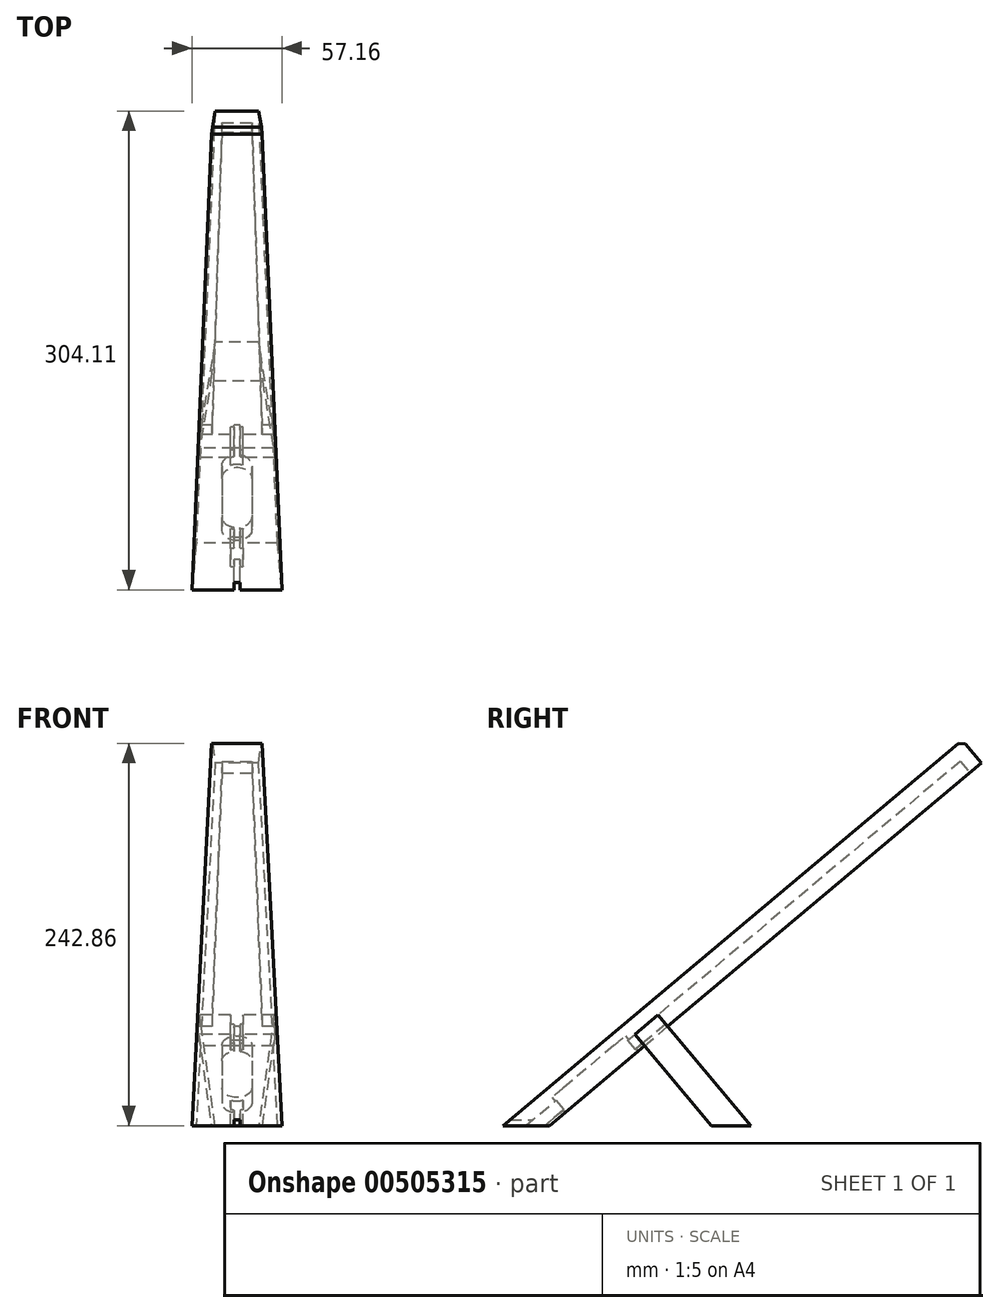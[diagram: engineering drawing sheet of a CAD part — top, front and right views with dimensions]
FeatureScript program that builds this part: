
annotation { "Feature Type Name" : "Feature", "Feature Type Description" : "" }
export const myFeature = defineFeature(function(context is Context, id is Id, definition is map)
    precondition{}
    {
        {
            var Q0;
            Q0=qCreatedBy(makeId("Right.planeOp"),FACE);
            var sketch = newSketch(context, id + "F0", { "sketchPlane" : qUnion([Q0])});
            skLineSegment(sketch, "E0", {"start": v(-81.13, 0) * mm, "end": v(210.73, 244.9) * mm});
            skLineSegment(sketch, "E1", {"start": v(210.73, 244.9) * mm, "end": v(222.98, 230.3) * mm});
            skLineSegment(sketch, "E2", {"start": v(222.98, 230.3) * mm, "end": v(23.54, 62.96) * mm});
            skLineSegment(sketch, "E3", {"start": v(-51.5, 0) * mm, "end": v(-81.13, 0) * mm});
            skLineSegment(sketch, "E4", {"start": v(8.94, 50.71) * mm, "end": v(51.5, 0) * mm});
            skLineSegment(sketch, "E5", {"start": v(51.5, 0) * mm, "end": v(76.36, 0) * mm});
            skLineSegment(sketch, "E6", {"start": v(76.36, 0) * mm, "end": v(23.54, 62.96) * mm});
            skLineSegment(sketch, "E7.trimOffspring", {"start": v(8.94, 50.71) * mm, "end": v(-51.5, 0) * mm});
            skLineSegment(sketch, "E8", {"start": v(-28.8, 19.05) * mm, "end": v(35.51, 19.05) * mm});
            skLineSegment(sketch, "E9", {"start": v(-51.5, 0) * mm, "end": v(51.5, 0) * mm});
            skLineSegment(sketch, "E10", {"start": v(35.51, 19.05) * mm, "end": v(60.38, 19.05) * mm});
            skLineSegment(sketch, "E11", {"start": v(-28.8, 19.05) * mm, "end": v(-58.43, 19.05) * mm});
            skLineSegment(sketch, "E12", {"start": v(23.54, 62.96) * mm, "end": v(17.41, 70.26) * mm});
            skLineSegment(sketch, "E13", {"start": v(17.41, 70.26) * mm, "end": v(2.82, 58.01) * mm});
            skLineSegment(sketch, "E14", {"start": v(8.94, 50.71) * mm, "end": v(2.82, 58.01) * mm});
            skSolve(sketch);
        }
        {
            var Q0;
            Q0=makeQuery(id+"F0.imprint","IMPRINT",FACE,{"disambiguationData":[TD([[makeQuery(id+"F0.imprint","IMPRINT",EDGE,{"derivedFrom":sQuery(id+"F0.wireOp",EDGE,"E0")}),-1.0]])]});
            var Q1;
            {var subQ0=sQuery(id+"F0.wireOp",EDGE,"E1");Q1=makeQuery(id+"F0.imprint","IMPRINT",FACE,{"disambiguationData":[TD([[makeQuery(id+"F0.imprint","IMPRINT",EDGE,{"derivedFrom":subQ0}),-1.0]])]});}
            extrude(context, id + "F1", {"entities" : qUnion([Q0, Q1]), "depth" : 57.15 * mm, "symmetric" : true});
        }
        {
            var Q0;
            Q0=makeQuery(id+"F0.imprint","IMPRINT",FACE,{"disambiguationData":[TD([[makeQuery(id+"F0.imprint","IMPRINT",EDGE,{"derivedFrom":sQuery(id+"F0.wireOp",EDGE,"E4")}),1.0]])]});
            var Q1;
            {var subQ1=sQuery(id+"F0.wireOp",EDGE,"EqHhwjUs-oOLM-PdHP-ePqw-IKI6tSrCbLh4");Q1=makeQuery(id+"F0.imprint","IMPRINT",FACE,{"disambiguationData":[TD([[makeQuery(id+"F0.imprint","IMPRINT",EDGE,{"derivedFrom":subQ1}),1.0]])]});}
            var Q2;
            {var subQ3=sQuery(id+"F0.wireOp",EDGE,"E10");Q2=makeQuery(id+"F0.imprint","IMPRINT",FACE,{"disambiguationData":[TD([[makeQuery(id+"F0.imprint","IMPRINT",EDGE,{"derivedFrom":subQ3}),1.0]])]});}
            extrude(context, id + "F2", {"entities" : qUnion([Q0, Q1, Q2]), "depth" : 57.15 * mm, "symmetric" : true});
        }
        {
            var Q0;
            Q0=makeQuery(id+"F1.opExtrude","SWEPT_FACE",FACE,{"disambiguationData":[OSD([sQuery(id+"F0.wireOp",EDGE,"E0")])]});
            var sketch = newSketch(context, id + "F3", { "sketchPlane" : qUnion([Q0])});
            skLineSegment(sketch, "E15", {"start": v(-15.87, 318.85) * mm, "end": v(-28.58, -62.15) * mm});
            skLineSegment(sketch, "E16", {"start": v(-28.58, -62.15) * mm, "end": v(-28.58, 318.85) * mm});
            skLineSegment(sketch, "E17", {"start": v(-28.58, 318.85) * mm, "end": v(-15.87, 318.85) * mm});
            skLineSegment(sketch, "E18.MirrorCS", {"start": v(15.87, 318.85) * mm, "end": v(28.58, -62.15) * mm});
            skLineSegment(sketch, "E19.MirrorCS", {"start": v(28.58, 318.85) * mm, "end": v(15.87, 318.85) * mm});
            skLineSegment(sketch, "E20.MirrorCS", {"start": v(28.58, -62.15) * mm, "end": v(28.58, 318.85) * mm});
            skSolve(sketch);
        }
        {
            var Q0;
            Q0=makeQuery(id+"F1.opExtrude","SWEPT_FACE",FACE,{"disambiguationData":[OSD([sQuery(id+"F0.wireOp",EDGE,"E2")])]});
            var sketch = newSketch(context, id + "F4", { "sketchPlane" : qUnion([Q0])});
            skLineSegment(sketch, "E21", {"start": v(15.87, -58.5) * mm, "end": v(-15.87, -58.5) * mm});
            skLineSegment(sketch, "E22", {"start": v(-9.52, -309.32) * mm, "end": v(9.52, -309.32) * mm});
            skLineSegment(sketch, "E23", {"start": v(0, -318.85) * mm, "end": v(0, -309.32) * mm, "construction": true});
            skLineSegment(sketch, "E24", {"start": v(0, -309.32) * mm, "end": v(0, -318.85) * mm, "construction": true});
            skArc(sketch, "E25", {"start": v(-9.53, -24.69) * mm, "mid": v(0, -34.21) * mm, "end": v(9.53, -24.69) * mm});
            skArc(sketch, "E26", {"start": v(9.53, 17.22) * mm, "mid": v(0, 26.75) * mm, "end": v(-9.52, 17.22) * mm});
            skLineSegment(sketch, "E27", {"start": v(9.53, -24.69) * mm, "end": v(9.53, 17.22) * mm});
            skLineSegment(sketch, "E28", {"start": v(-9.53, -24.69) * mm, "end": v(-9.52, 17.22) * mm});
            skLineSegment(sketch, "E29", {"start": v(0, 17.22) * mm, "end": v(0, 39.45) * mm, "construction": true});
            skLineSegment(sketch, "E30", {"start": v(1.9, 64.45) * mm, "end": v(-1.9, 64.45) * mm});
            skLineSegment(sketch, "E31", {"start": v(1.9, 64.45) * mm, "end": v(1.9, 26.56) * mm});
            skLineSegment(sketch, "E32", {"start": v(-1.9, 64.45) * mm, "end": v(-1.9, 26.56) * mm});
            skPoint(sketch, "E33.orphan", {"position": v(1.9, 0) * mm});
            skLineSegment(sketch, "E34", {"start": v(1.9, -34.02) * mm, "end": v(1.9, -58.5) * mm});
            skLineSegment(sketch, "E35", {"start": v(-1.9, -34.02) * mm, "end": v(-1.9, -58.5) * mm});
            skLineSegment(sketch, "E36", {"start": v(9.52, -309.32) * mm, "end": v(15.87, -58.5) * mm});
            skLineSegment(sketch, "E37", {"start": v(-9.52, -309.32) * mm, "end": v(-15.87, -58.5) * mm});
            skLineSegment(sketch, "E38", {"start": v(0, -309.32) * mm, "end": v(0, -58.5) * mm, "construction": true});
            skSolve(sketch);
        }
        {
            var Q0;
            Q0=makeQuery(id+"F4.imprint","IMPRINT",FACE,{"disambiguationData":[TD([[makeQuery(id+"F4.imprint","IMPRINT",EDGE,{"derivedFrom":sQuery(id+"F4.wireOp",EDGE,"E22")}),1.0]])]});
            extrude(context, id + "F5", {"entities" : qUnion([Q0]), "operationType" : NewBodyOperationType.REMOVE, "oppositeDirection" : true, "depth" : 9.52 * mm, "offsetDistance" : 25.4 * mm});
        }
        {
            var Q0;
            Q0=makeQuery(id+"F3.imprint","IMPRINT",FACE,{"disambiguationData":[TD([[makeQuery(id+"F3.imprint","IMPRINT",EDGE,{"derivedFrom":sQuery(id+"F3.wireOp",EDGE,"E18.MirrorCS")}),1.0]])]});
            var Q1;
            Q1=makeQuery(id+"F3.imprint","IMPRINT",FACE,{"disambiguationData":[TD([[makeQuery(id+"F3.imprint","IMPRINT",EDGE,{"derivedFrom":sQuery(id+"F3.wireOp",EDGE,"E15")}),-1.0]])]});
            extrude(context, id + "F6", {"entities" : qUnion([Q0, Q1]), "operationType" : NewBodyOperationType.REMOVE, "endBound" : BoundingType.THROUGH_ALL, "oppositeDirection" : true, "depth" : 25.4 * mm, "hasDraft" : true, "draftAngle" : 6 * degree});
        }
        {
            var Q0;
            Q0=makeQuery(id+"F4.imprint","IMPRINT",FACE,{"disambiguationData":[TD([[makeQuery(id+"F4.imprint","IMPRINT",EDGE,{"derivedFrom":sQuery(id+"F4.wireOp",EDGE,"E30")}),1.0]])]});
            var Q1;
            {var subQ0=sQuery(id+"F4.wireOp",EDGE,"E34");var subQ1=sQuery(id+"F4.wireOp",EDGE,"E25");var subQ2=makeQuery(id+"F4.imprint","INTERSECT",VERTEX,{"derivedFrom":[subQ1,subQ0]});Q1=makeQuery(id+"F4.imprint","IMPRINT",FACE,{"disambiguationData":[TD([[makeQuery(id+"F4.imprint","IMPRINT",EDGE,{"disambiguationData":[TD([[subQ2,1.0]])],"derivedFrom":subQ1}),-1.0]])]});}
            var Q2;
            {var subQ0=sQuery(id+"F4.wireOp",EDGE,"E34");var subQ1=sQuery(id+"F4.wireOp",EDGE,"E21");var subQ2=makeQuery(id+"F4.imprint","INTERSECT",VERTEX,{"derivedFrom":[subQ1,subQ0]});Q2=makeQuery(id+"F4.imprint","IMPRINT",FACE,{"disambiguationData":[TD([[makeQuery(id+"F4.imprint","IMPRINT",EDGE,{"disambiguationData":[TD([[subQ2,-1.0]])],"derivedFrom":subQ1}),-1.0]])]});}
            extrude(context, id + "F7", {"entities" : qUnion([Q0, Q1, Q2]), "operationType" : NewBodyOperationType.REMOVE, "oppositeDirection" : true, "depth" : 9.52 * mm, "offsetDistance" : 25.4 * mm});
        }
        {
            var Q0;
            Q0=makeQuery(id+"F4.imprint","IMPRINT",FACE,{"disambiguationData":[TD([[makeQuery(id+"F4.imprint","IMPRINT",EDGE,{"derivedFrom":sQuery(id+"F4.wireOp",EDGE,"E25")}),1.0]])]});
            extrude(context, id + "F8", {"entities" : qUnion([Q0]), "operationType" : NewBodyOperationType.REMOVE, "oppositeDirection" : true, "depth" : 12.7 * mm, "offsetDistance" : 25.4 * mm});
        }
        {
            var Q0;
            Q0=makeQuery(id+"F6.boolean.opBoolean","COPY",EDGE,{"derivedFrom":makeQuery(id+"F6.opExtrude","CAP_EDGE",EDGE,{"disambiguationData":[OSD([sQuery(id+"F3.wireOp",EDGE,"E18.MirrorCS")])],"isStart":true})});
            var Q1;
            Q1=makeQuery(id+"F1.opExtrude","SWEPT_EDGE",EDGE,{"disambiguationData":[OSD([sQuery(id+"F0.wireOp",EDGE,"E0"),sQuery(id+"F0.wireOp",EDGE,"E1")])]});
            var Q2;
            Q2=makeQuery(id+"F6.boolean.opBoolean","COPY",EDGE,{"derivedFrom":makeQuery(id+"F6.opExtrude","CAP_EDGE",EDGE,{"disambiguationData":[OSD([sQuery(id+"F3.wireOp",EDGE,"E15")])],"isStart":true})});
            chamfer(context, id + "F9", {"entities" : qUnion([Q0, Q1, Q2]), "width" : 3.17 * mm, "tangentPropagation" : true});
        }
        {
            var Q0;
            Q0=qCreatedBy(makeId("Front.planeOp"),FACE);
            var sketch = newSketch(context, id + "F10", { "sketchPlane" : qUnion([Q0])});
            skLineSegment(sketch, "E39", {"start": v(0, 0) * mm, "end": v(0, 20.46) * mm, "construction": true});
            skLineSegment(sketch, "E40", {"start": v(-1.9, 3.81) * mm, "end": v(-1.9, 0) * mm});
            skLineSegment(sketch, "E41", {"start": v(1.9, 3.81) * mm, "end": v(1.9, 0) * mm});
            skLineSegment(sketch, "E42", {"start": v(-1.9, 0) * mm, "end": v(1.9, 0) * mm});
            skLineSegment(sketch, "E43", {"start": v(1.9, 3.81) * mm, "end": v(-1.9, 3.81) * mm});
            skPoint(sketch, "E44.center.orphan", {"position": v(0, 3.81) * mm});
            skSolve(sketch);
        }
        {
            var Q0;
            Q0=makeQuery(id+"F10.imprint","IMPRINT",FACE,{"disambiguationData":[TD([[makeQuery(id+"F10.imprint","IMPRINT",EDGE,{"derivedFrom":sQuery(id+"F10.wireOp",EDGE,"E40")}),1.0]])]});
            extrude(context, id + "F11", {"entities" : qUnion([Q0]), "operationType" : NewBodyOperationType.REMOVE, "endBound" : BoundingType.THROUGH_ALL, "depth" : 25.4 * mm, "offsetDistance" : 25.4 * mm});
        }
        {
            var Q0;
            Q0=makeQuery(id+"F2.opExtrude","SWEPT_FACE",FACE,{"disambiguationData":[OSD([sQuery(id+"F0.wireOp",EDGE,"E6"),sQuery(id+"F0.wireOp",EDGE,"E12")])]});
            var sketch = newSketch(context, id + "F12", { "sketchPlane" : qUnion([Q0])});
            skLineSegment(sketch, "E45.bottom", {"start": v(-4, 36.28) * mm, "end": v(4, 36.28) * mm});
            skLineSegment(sketch, "E45.top", {"start": v(-4, 35) * mm, "end": v(4, 35) * mm});
            skLineSegment(sketch, "E45.left", {"start": v(-4, 36.28) * mm, "end": v(-4, 35) * mm});
            skLineSegment(sketch, "E45.right", {"start": v(4, 36.28) * mm, "end": v(4, 35) * mm});
            skLineSegment(sketch, "E46.top", {"start": v(-4, 42.63) * mm, "end": v(4, 42.63) * mm});
            skLineSegment(sketch, "E46.left", {"start": v(-4, 36.28) * mm, "end": v(-4, 42.63) * mm});
            skLineSegment(sketch, "E46.right", {"start": v(4, 36.28) * mm, "end": v(4, 42.63) * mm});
            skSolve(sketch);
        }
        {
            var Q0;
            Q0 = qSketchRegion(id + "F12", true);
            extrude(context, id + "F13", {"entities" : qUnion([Q0]), "operationType" : NewBodyOperationType.REMOVE, "endBound" : BoundingType.THROUGH_ALL, "oppositeDirection" : true, "depth" : 25.4 * mm, "offsetDistance" : 25.4 * mm});
        }
    });
